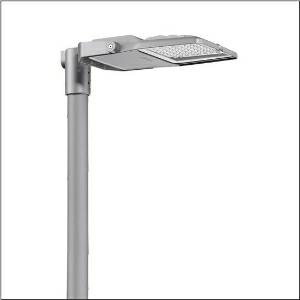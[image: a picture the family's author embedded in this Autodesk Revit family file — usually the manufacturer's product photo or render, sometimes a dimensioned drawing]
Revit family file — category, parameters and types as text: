
# Revit family: floodlight_fl_21_mini___pl33t_5xa7771d2f3a_4180
name_source: partatom
category: Lighting Fixtures
units: mm (PartAtom-declared; Revit-internal decimal feet)

## family parameters
Cut with Voids When Loaded = No
Host = Face
Light Source = No
Part Type = Normal
Room Calculation Point = No
Round Connector Dimension = Use Diameter
Shared = No

## types (1)
- --- (1 x LED, 17620 lm, 143 W, 3000K)
    Apparent Load = 143 VA
    CIE Flux Codes = 26 75 99 100 100
    Color Rendering = 70
    Color Temperature = 3000K
    Default Elevation = 1800 mm
    Description = Floodlight FL 21 mini, floodlight, primary light control with lens, of PMMA, primary optical cover: protective disc, of toughened safety glass, transparent, light distribution: PL33T, light emission: direct distribution, installation type: surface-mounted, LED, High Power LED, rated luminous flux: 17.620lm, luminous efficacy: 123lm/W, light colour: 730, colour temperature: 3000K, control gear: ECG iQ, control: Auto-Match, Temp-Guard, Lumen-Switch, Night-Set, Smart-Wire, Light-Fading, Desk-Remote (wireless, voltage-free reading and setting of iQ features in the workshop via application-optimized NFC function/RFID function), optimised constant luminous flux control (CLO 2.0), with terminal, 6-pole, mains connection: 220..240V, AC, 50/60Hz, start of lifetime: 143W, end of lifetime: 152W, reduction: 61W, luminaire housing, of diecast aluminium, powder-coated, Siteco® metallic grey (DB 702S), corrosivity category C5 according to DIN EN ISO 12944, mast bracket, of steel, galvanised, powder-coated, Siteco® metallic grey (DB 702S), protection rating (complete): IP66, insulation class (complete): insulation class II (safety insulation), certification: CE, ENEC, VDE, protection symbol: D, impact resistance: IK08, permissible operating ambient temperature: -40..+40°C, permissible operating ambient temperature for outdoor applications: -40..+50°C, standard: DIN EN 12944, packaging unit: 1 piece

Light Distribution: PL33T
    Height = 70 mm
    Lamp = 1 x LED
    Lamp Light Flux = 17620 lm
    Lamp Power = 143 W
    Lamp count = 1
    Length = 485 mm
    Luminous efficacy = 123 lm/W
    Manufacturer = Siteco
    ModVariant = No
    Model = 5XA7771D2F3A
    Number of Poles = 1
    OnlyDefault = Yes
    Power Factor = 1
    Product Name = Floodlight FL 21 mini | PL33T
    Product group = floodlight | pylon top
    ProductGroupID = 6101
    Protection Class = Protection class II
    Protection Degree = IP 66
    RLX_Detail_Level = 1
    RlxData = <blob elided: 101301 chars, md5=5f04a90f>
    Socket = socket
    Standby Power = 0 W
    System Light Flux = 17620 lm
    System Power = 143 W
    Type Comments = factory setting: luminous flux: 100 % | dim-lin: 254 | 730 mA
    Type Image = l_1007125.jpg
    URL = http://relux.com
    VarID = @adj_059219
    Voltage = 0 V
    Weight = 0.00 kg
    Width = 337 mm

## geometry (parser evidence)
native form markers: Blend x4, Sweep x12
no freeform markers — native parametric forms only
